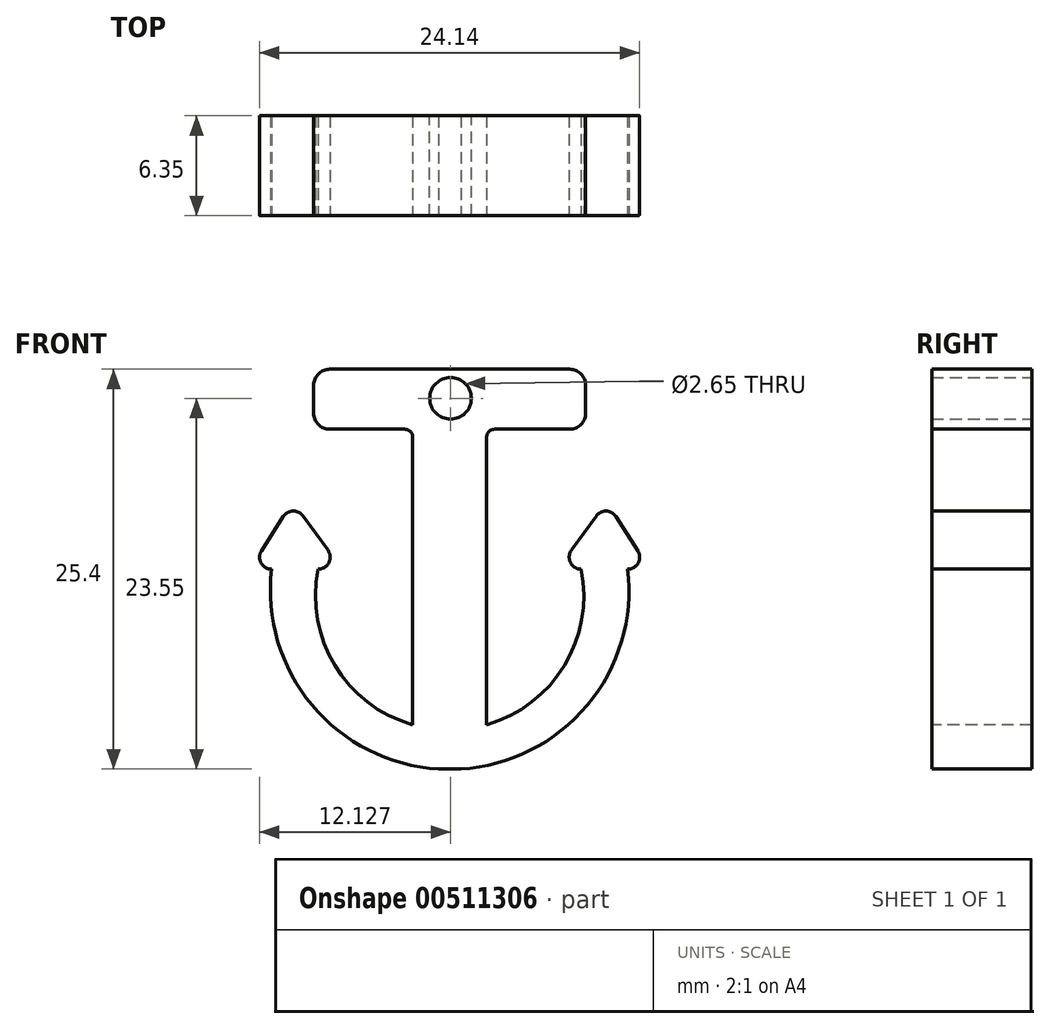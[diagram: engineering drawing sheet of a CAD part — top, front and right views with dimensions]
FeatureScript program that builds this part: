
annotation { "Feature Type Name" : "Feature", "Feature Type Description" : "" }
export const myFeature = defineFeature(function(context is Context, id is Id, definition is map)
    precondition{}
    {
        {
            var Q0;
            Q0=qCreatedBy(makeId("Front.planeOp"),FACE);
            var sketch = newSketch(context, id + "F0", { "sketchPlane" : qUnion([Q0])});
            skLineSegment(sketch, "E0.bottom", {"start": v(0, 0) * mm, "end": v(25.4, 0) * mm});
            skLineSegment(sketch, "E0.top", {"start": v(0, 25.4) * mm, "end": v(25.4, 25.4) * mm});
            skLineSegment(sketch, "E0.left", {"start": v(0, 0) * mm, "end": v(0, 25.4) * mm});
            skLineSegment(sketch, "E0.right", {"start": v(25.4, 0) * mm, "end": v(25.4, 25.4) * mm});
            skSolve(sketch);
        }
        {
            var Q0;
            Q0 = qSketchRegion(id + "F0", true);
            var Q1;
            Q1 = qSketchRegion(id + "F2", true);
            extrude(context, id + "F1", {"entities" : qUnion([Q0, Q1]), "depth" : 6.35 * mm, "offsetDistance" : 25.4 * mm});
        }
        {
            var Q0;
            Q0=makeQuery(id+"F1.opExtrude","CAP_FACE",FACE,{"disambiguationData":[OSD([sQuery(id+"F0.wireOp",EDGE,"E0.bottom"),sQuery(id+"F0.wireOp",EDGE,"E0.top"),sQuery(id+"F0.wireOp",EDGE,"E0.left"),sQuery(id+"F0.wireOp",EDGE,"E0.right")])],"isStart":false});
            var sketch = newSketch(context, id + "F2", { "sketchPlane" : qUnion([Q0])});
            skLineSegment(sketch, "E1", {"start": v(10.35, 2.81) * mm, "end": v(10.35, 21.08) * mm});
            skLineSegment(sketch, "E2", {"start": v(15.05, 2.81) * mm, "end": v(15.05, 15.5) * mm});
            skLineSegment(sketch, "E3", {"start": v(15.05, 15.5) * mm, "end": v(15.05, 21.08) * mm});
            skLineSegment(sketch, "E4", {"start": v(20.32, 21.59) * mm, "end": v(15.56, 21.59) * mm});
            skLineSegment(sketch, "E5", {"start": v(4.06, 22.6) * mm, "end": v(4.06, 24.38) * mm});
            skLineSegment(sketch, "E6", {"start": v(5.08, 25.4) * mm, "end": v(20.32, 25.4) * mm});
            skLineSegment(sketch, "E7", {"start": v(21.34, 24.38) * mm, "end": v(21.34, 22.6) * mm});
            skLineSegment(sketch, "E8", {"start": v(22, 16.08) * mm, "end": v(20.44, 13.9) * mm});
            skLineSegment(sketch, "E9", {"start": v(23.27, 16.04) * mm, "end": v(24.65, 13.87) * mm});
            skLineSegment(sketch, "E10", {"start": v(2.13, 16.04) * mm, "end": v(0.75, 13.87) * mm});
            skLineSegment(sketch, "E11", {"start": v(3.4, 16.08) * mm, "end": v(4.96, 13.9) * mm});
            skPoint(sketch, "E12.visualSharp", {"position": v(21.34, 21.59) * mm});
            skArc(sketch, "E12.filletArc", {"start": v(20.32, 21.59) * mm, "mid": v(21.04, 21.89) * mm, "end": v(21.34, 22.6) * mm});
            skPoint(sketch, "E13.visualSharp", {"position": v(4.06, 21.59) * mm});
            skArc(sketch, "E13.filletArc", {"start": v(4.06, 22.6) * mm, "mid": v(4.36, 21.89) * mm, "end": v(5.08, 21.59) * mm});
            skPoint(sketch, "E14.visualSharp", {"position": v(4.06, 25.4) * mm});
            skArc(sketch, "E14.filletArc", {"start": v(5.08, 25.4) * mm, "mid": v(4.36, 25.1) * mm, "end": v(4.06, 24.38) * mm});
            skPoint(sketch, "E15.visualSharp", {"position": v(21.34, 25.4) * mm});
            skArc(sketch, "E15.filletArc", {"start": v(21.34, 24.38) * mm, "mid": v(21.04, 25.1) * mm, "end": v(20.32, 25.4) * mm});
            skPoint(sketch, "E16.visualSharp", {"position": v(2.73, 16.98) * mm});
            skArc(sketch, "E16.filletArc", {"start": v(3.4, 16.08) * mm, "mid": v(2.75, 16.4) * mm, "end": v(2.13, 16.04) * mm});
            skPoint(sketch, "E17.visualSharp", {"position": v(5.84, 12.7) * mm});
            skArc(sketch, "E17.filletArc", {"start": v(4.35, 12.7) * mm, "mid": v(5.03, 13.12) * mm, "end": v(4.96, 13.9) * mm});
            skPoint(sketch, "E18.visualSharp", {"position": v(0, 12.7) * mm});
            skArc(sketch, "E18.filletArc", {"start": v(0.75, 13.87) * mm, "mid": v(0.72, 13.1) * mm, "end": v(1.4, 12.7) * mm});
            skPoint(sketch, "E19.visualSharp", {"position": v(19.56, 12.7) * mm});
            skArc(sketch, "E19.filletArc", {"start": v(20.44, 13.9) * mm, "mid": v(20.37, 13.12) * mm, "end": v(21.05, 12.7) * mm});
            skPoint(sketch, "E20.visualSharp", {"position": v(22.67, 16.98) * mm});
            skArc(sketch, "E20.filletArc", {"start": v(23.27, 16.04) * mm, "mid": v(22.65, 16.4) * mm, "end": v(22, 16.08) * mm});
            skPoint(sketch, "E21.visualSharp", {"position": v(25.4, 12.7) * mm});
            skArc(sketch, "E21.filletArc", {"start": v(24, 12.7) * mm, "mid": v(24.68, 13.1) * mm, "end": v(24.65, 13.87) * mm});
            skLineSegment(sketch, "E22.trimOffspring", {"start": v(9.84, 21.59) * mm, "end": v(5.08, 21.59) * mm});
            skPoint(sketch, "E23.visualSharp", {"position": v(10.35, 21.59) * mm});
            skArc(sketch, "E23.filletArc", {"start": v(10.35, 21.08) * mm, "mid": v(10.2, 21.44) * mm, "end": v(9.84, 21.59) * mm});
            skPoint(sketch, "E24.visualSharp", {"position": v(15.05, 21.59) * mm});
            skArc(sketch, "E24.filletArc", {"start": v(15.56, 21.59) * mm, "mid": v(15.2, 21.44) * mm, "end": v(15.05, 21.08) * mm});
            skArc(sketch, "E25", {"start": v(1.4, 12.7) * mm, "mid": v(12.7, -0.02) * mm, "end": v(24, 12.7) * mm});
            skArc(sketch, "E26", {"start": v(4.35, 12.7) * mm, "mid": v(5.41, 6.58) * mm, "end": v(10.35, 2.81) * mm});
            skArc(sketch, "E27.trimOffspring", {"start": v(15.05, 2.81) * mm, "mid": v(19.99, 6.58) * mm, "end": v(21.05, 12.7) * mm});
            skSolve(sketch);
        }
        {
            var Q0;
            Q0=makeQuery(id+"F2.imprint","IMPRINT",FACE,{"disambiguationData":[TD([[makeQuery(id+"F2.imprint","IMPRINT",EDGE,{"derivedFrom":sQuery(id+"F2.wireOp",EDGE,"E1")}),1.0]])]});
            var Q1;
            Q1=makeQuery(id+"F2.imprint","IMPRINT",FACE,{"disambiguationData":[TD([[makeQuery(id+"F2.imprint","IMPRINT",EDGE,{"derivedFrom":sQuery(id+"F2.wireOp",EDGE,"E2")}),-1.0]])]});
            extrude(context, id + "F3", {"entities" : qUnion([Q0, Q1]), "operationType" : NewBodyOperationType.REMOVE, "oppositeDirection" : true, "depth" : 25.4 * mm, "offsetDistance" : 25.4 * mm});
        }
        {
            var Q0;
            Q0=qCreatedBy(makeId("Front.planeOp"),FACE);
            var sketch = newSketch(context, id + "F4", { "sketchPlane" : qUnion([Q0])});
            skLineSegment(sketch, "E28", {"start": v(12.76, 22.73) * mm, "end": v(12.76, 24.37) * mm});
            skCircle(sketch, "E29", {"center": v(12.76, 23.55) * mm, "radius": 1.32 * mm});
            skSolve(sketch);
        }
        {
            var Q0;
            Q0 = qSketchRegion(id + "F4", true);
            extrude(context, id + "F5", {"entities" : qUnion([Q0]), "operationType" : NewBodyOperationType.REMOVE, "depth" : 25.4 * mm, "offsetDistance" : 25.4 * mm});
        }
    });
